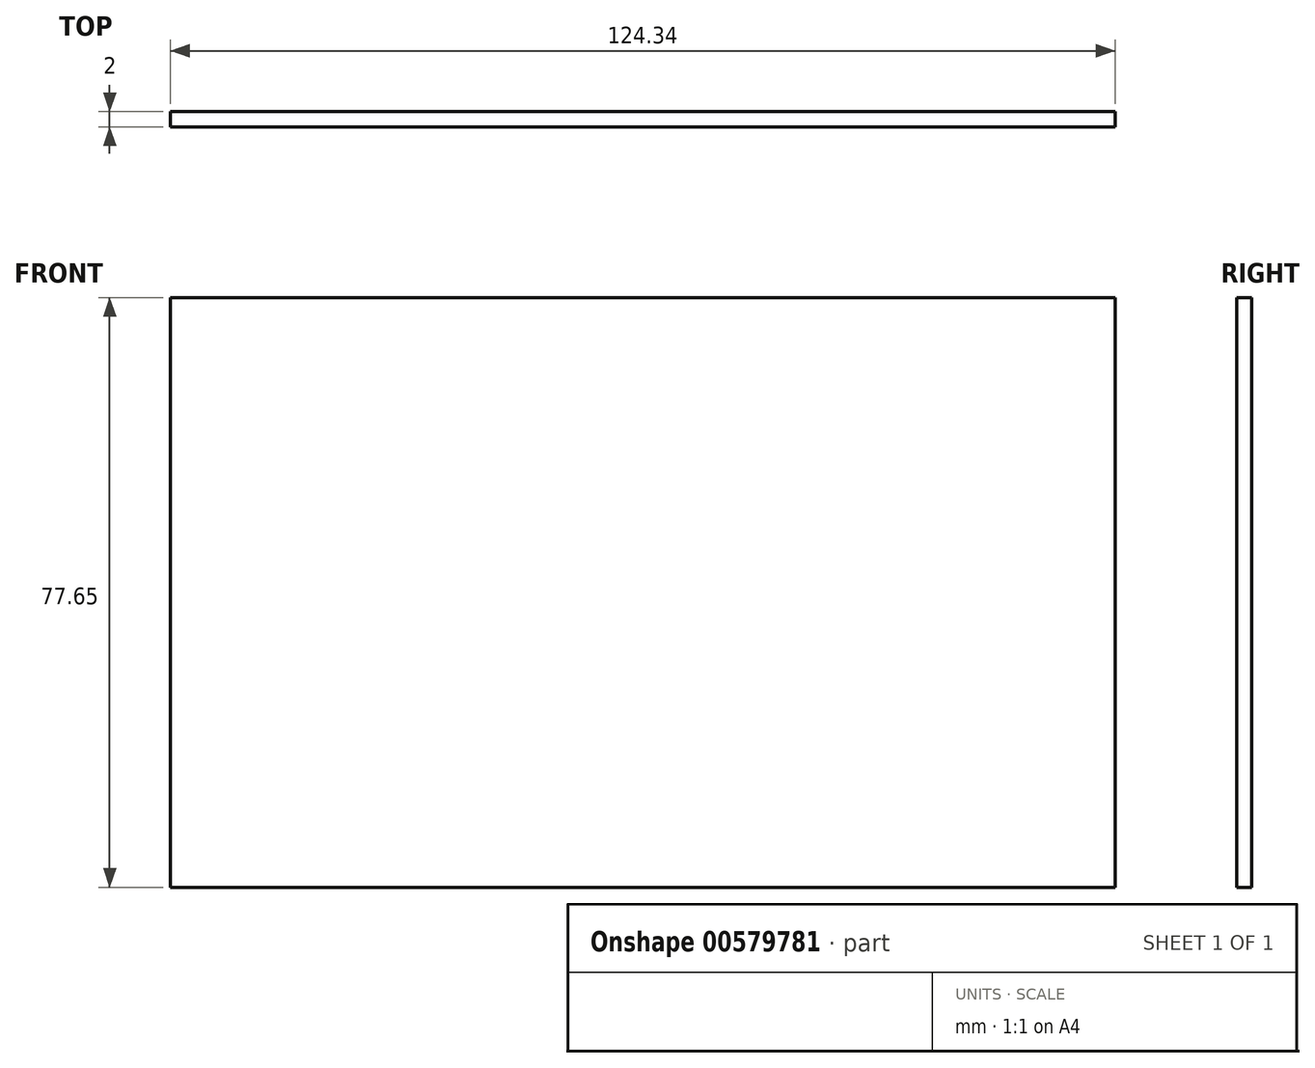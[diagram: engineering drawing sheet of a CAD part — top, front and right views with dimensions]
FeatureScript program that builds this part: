
annotation { "Feature Type Name" : "Feature", "Feature Type Description" : "" }
export const myFeature = defineFeature(function(context is Context, id is Id, definition is map)
    precondition{}
    {
        {
            var Q0;
            Q0=qCreatedBy(makeId("Front.planeOp"),FACE);
            var sketch = newSketch(context, id + "F0", { "sketchPlane" : qUnion([Q0])});
            skLineSegment(sketch, "E0.bottom", {"start": v(-59.06, 37.1) * mm, "end": v(65.28, 37.1) * mm});
            skLineSegment(sketch, "E0.top", {"start": v(-59.06, -40.55) * mm, "end": v(65.28, -40.55) * mm});
            skLineSegment(sketch, "E0.left", {"start": v(-59.06, 37.1) * mm, "end": v(-59.06, -40.55) * mm});
            skLineSegment(sketch, "E0.right", {"start": v(65.28, 37.1) * mm, "end": v(65.28, -40.55) * mm});
            skSolve(sketch);
        }
        {
            var Q0;
            Q0=makeQuery(id+"F0.imprint","IMPRINT",FACE,{"disambiguationData":[TD([[makeQuery(id+"F0.imprint","IMPRINT",EDGE,{"derivedFrom":sQuery(id+"F0.wireOp",EDGE,"E0.bottom")}),-1.0]])]});
            extrude(context, id + "F1", {"entities" : qUnion([Q0]), "depth" : 2 * mm, "offsetDistance" : 25 * mm});
        }
    });
